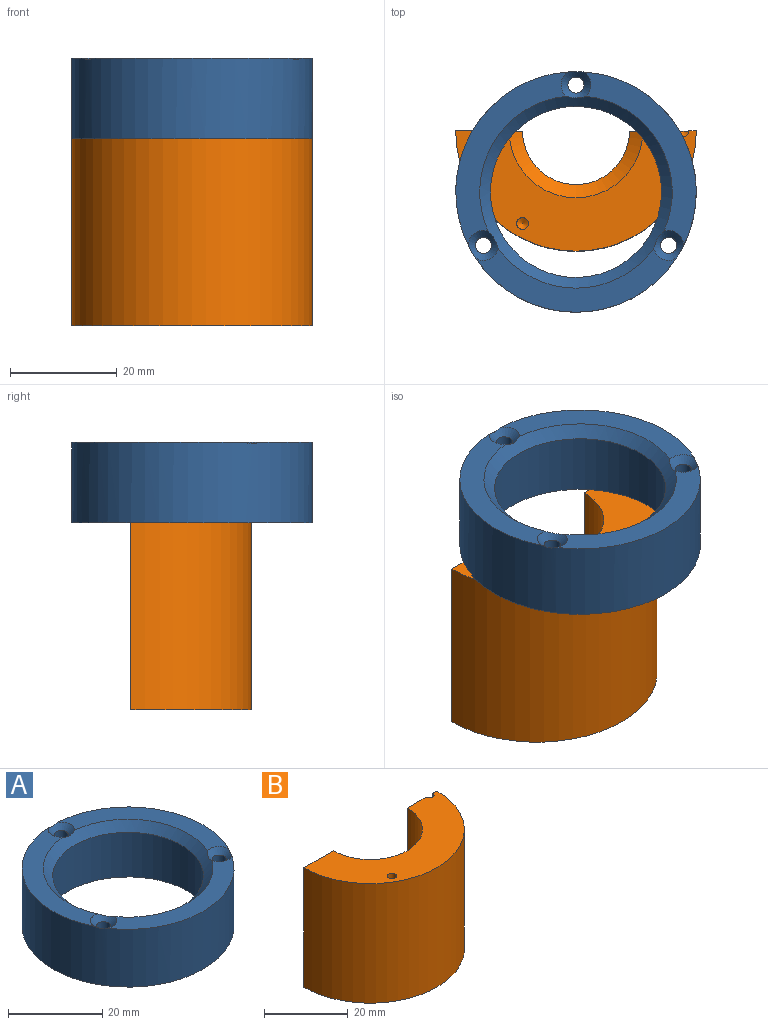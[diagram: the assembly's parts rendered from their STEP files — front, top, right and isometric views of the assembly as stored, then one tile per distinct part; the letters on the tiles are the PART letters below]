
ASSEMBLY  parts=2 mates=1
PART A: 14 faces, bbox 45x45.3x15 mm
  f0: cylinder r=22.5mm len=45mm, axis (0,0,-1), area 2119mm2, adj f1,f2,f4,f5,f8,f10,f12
  f1: plane 37.57x11.94mm, normal (0,0,1), area 168.8mm2, adj f0,f3,f10,f12
  f2: plane 32.53x21.16mm, normal (0,0,1), area 168.8mm2, adj f0,f3,f8,f12
  f3: cone r=16mm half-angle=45deg, axis (0,0,1), area 297.9mm2, adj f1,f2,f4,f7,f8,f10,f12
  f4: plane 32.53x21.16mm, normal (0,0,1), area 168.8mm2, adj f0,f3,f8,f10
  f5: plane 45x45mm, normal (0,0,-1), area 551.3mm2, adj f0,f6,f9,f11,f13
  f6: cylinder r=18mm len=36mm, axis (0,0,-1), area 1470.3mm2, adj f5,f7
  f7: plane 36x36mm, normal (0,0,-1), area 213.6mm2, adj f3,f6
  f8: cone r=1.5mm half-angle=45deg, axis (0,0,1), area 22.6mm2, adj f0,f2,f3,f4,f9
  f9: cylinder r=1.5mm len=13.7mm, axis (0,0,1), area 129.1mm2, adj f5,f8
  f10: cone r=1.5mm half-angle=45deg, axis (0,0,1), area 22.6mm2, adj f0,f1,f3,f4,f11
  f11: cylinder r=1.5mm len=13.7mm, axis (0,0,1), area 129.1mm2, adj f5,f10
  f12: cone r=1.5mm half-angle=45deg, axis (0,0,1), area 22.6mm2, adj f0,f1,f2,f3,f13
  f13: cylinder r=1.5mm len=13.7mm, axis (0,0,1), area 129.1mm2, adj f5,f12
PART B: 14 faces, bbox 45x22.5x35 mm
  f0: cone r=0mm half-angle=59deg, axis (0,0,1), area 103.1mm2, adj f6,f7,f12,f13
  f1: cylinder r=22.5mm len=45mm, axis (0,0,-1), area 2474mm2, adj f2,f3,f12,f13
  f2: plane 45x22.5mm, normal (0,0,1), area 544.1mm2, adj f1,f6,f8,f10,f12,f13
  f3: plane 45x22.5mm, normal (0,0,-1), area 286.3mm2, adj f1,f4,f12,f13
  f4: cylinder r=18mm len=36mm, axis (0,0,-1), area 452.4mm2, adj f3,f5,f12,f13
  f5: plane 36x18mm, normal (0,0,-1), area 351.9mm2, adj f4,f7,f12,f13
  f6: cylinder r=12.5mm len=25mm, axis (0,0,1), area 785.4mm2, adj f0,f2,f12,f13
  f7: cylinder r=10mm len=20mm, axis (0,0,1), area 172.7mm2, adj f0,f5,f12,f13
  f8: cylinder r=1.1mm len=15mm, axis (0,0,1), area 51.8mm2, adj f2,f9,f12
  f9: cone r=0mm half-angle=59deg, axis (0,0,1), area 2.2mm2, adj f8,f12
  f10: cylinder r=1.1mm len=15mm, axis (0,0,1), area 103.7mm2, adj f2,f11
  f11: cone r=0mm half-angle=59deg, axis (0,0,1), area 4.4mm2, adj f10
  f12: plane 35x12.5mm, normal (0,1,0), area 287.9mm2, adj f0,f1,f2,f3,f4,f5,f6,f7
  f13: plane 35x12.5mm, normal (0,1,0), area 321.6mm2, adj f0,f1,f2,f3,f4,f5,f6,f7
PLACE A t=(-20.36,-12.19,26.57)mm
PLACE B t=(-20.36,-0.75,-8.43)mm
MATE revolute A.f0 <-> B.f2  axis (0,0,-1) through (-20.36,-12.19,26.57)mm
